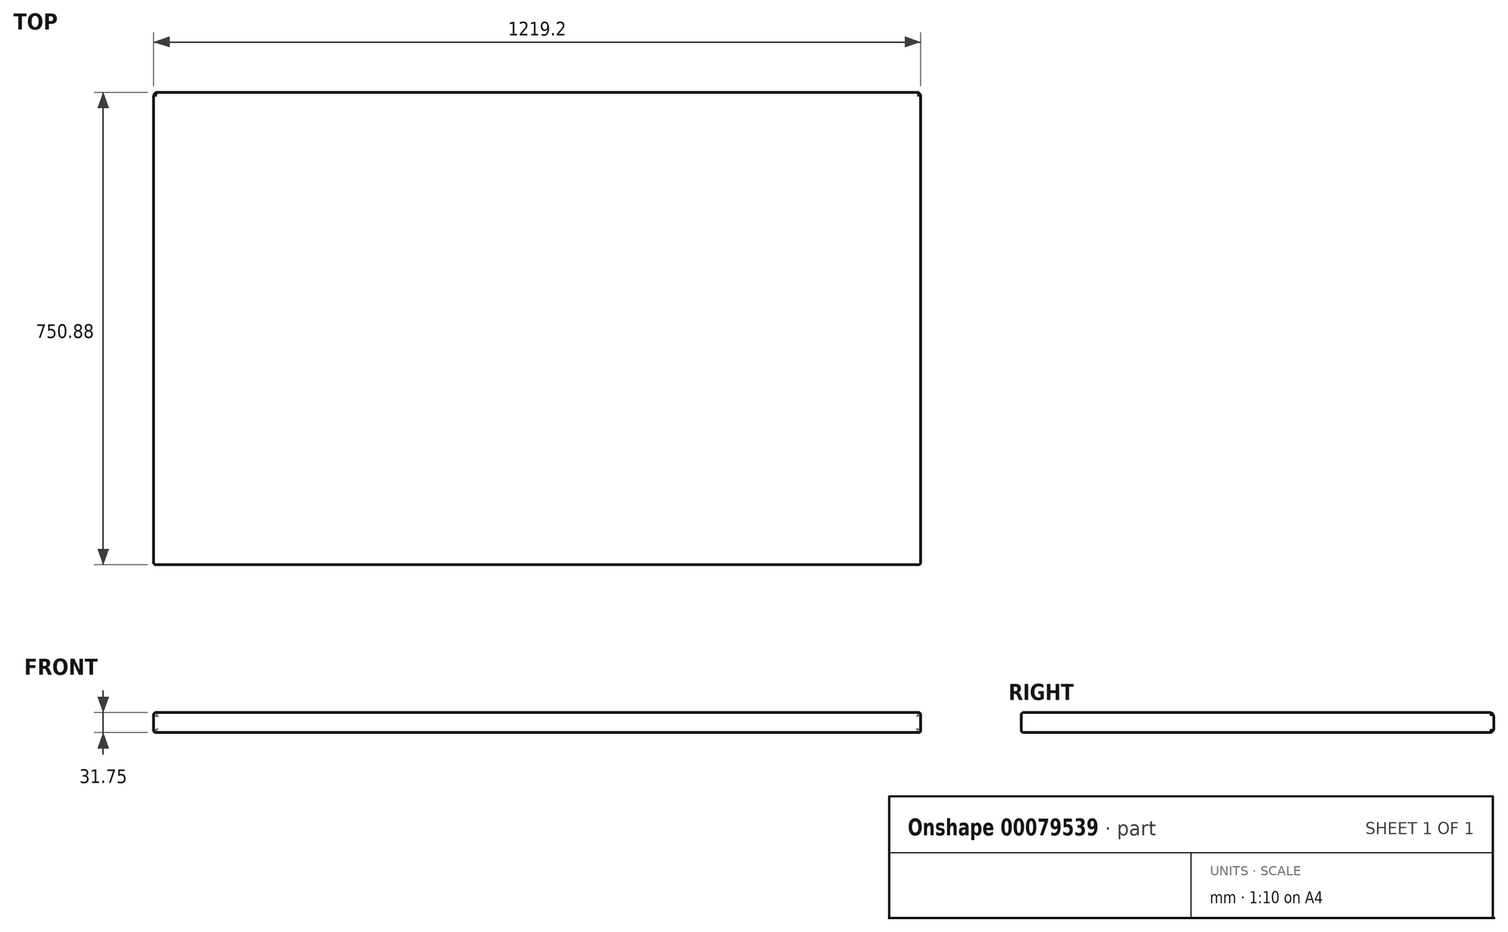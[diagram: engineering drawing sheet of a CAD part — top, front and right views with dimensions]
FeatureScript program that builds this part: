
annotation { "Feature Type Name" : "Feature", "Feature Type Description" : "" }
export const myFeature = defineFeature(function(context is Context, id is Id, definition is map)
    precondition{}
    {
        {
            var Q0;
            Q0=qCreatedBy(makeId("Top.planeOp"),FACE);
            var sketch = newSketch(context, id + "F0", { "sketchPlane" : qUnion([Q0])});
            skLineSegment(sketch, "E0.bottom", {"start": v(609.6, -375.44) * mm, "end": v(-609.6, -375.44) * mm});
            skLineSegment(sketch, "E0.top", {"start": v(609.6, 375.44) * mm, "end": v(-609.6, 375.44) * mm});
            skLineSegment(sketch, "E0.left", {"start": v(609.6, -375.44) * mm, "end": v(609.6, 375.44) * mm});
            skLineSegment(sketch, "E0.right", {"start": v(-609.6, -375.44) * mm, "end": v(-609.6, 375.44) * mm});
            skPoint(sketch, "E0.middle", {"position": v(0, 0) * mm});
            skSolve(sketch);
        }
        {
            var Q0;
            Q0=makeQuery(id+"F0.imprint","IMPRINT",FACE,{"disambiguationData":[TD([[makeQuery(id+"F0.imprint","IMPRINT",EDGE,{"derivedFrom":sQuery(id+"F0.wireOp",EDGE,"E0.bottom")}),-1.0]])]});
            extrude(context, id + "F1", {"entities" : qUnion([Q0]), "depth" : 31.75 * mm});
        }
        {
            var Q0;
            Q0=makeQuery(id+"F1.opExtrude","CAP_EDGE",EDGE,{"disambiguationData":[OSD([sQuery(id+"F0.wireOp",EDGE,"E0.right")])],"isStart":false});
            var Q1;
            Q1=makeQuery(id+"F1.opExtrude","CAP_EDGE",EDGE,{"disambiguationData":[OSD([sQuery(id+"F0.wireOp",EDGE,"E0.bottom")])],"isStart":false});
            var Q2;
            Q2=makeQuery(id+"F1.opExtrude","CAP_EDGE",EDGE,{"disambiguationData":[OSD([sQuery(id+"F0.wireOp",EDGE,"E0.left")])],"isStart":false});
            var Q3;
            Q3=makeQuery(id+"F1.opExtrude","CAP_EDGE",EDGE,{"disambiguationData":[OSD([sQuery(id+"F0.wireOp",EDGE,"E0.left")])],"isStart":true});
            var Q4;
            Q4=makeQuery(id+"F1.opExtrude","CAP_EDGE",EDGE,{"disambiguationData":[OSD([sQuery(id+"F0.wireOp",EDGE,"E0.bottom")])],"isStart":true});
            var Q5;
            Q5=makeQuery(id+"F1.opExtrude","CAP_EDGE",EDGE,{"disambiguationData":[OSD([sQuery(id+"F0.wireOp",EDGE,"E0.right")])],"isStart":true});
            var Q6;
            Q6=makeQuery(id+"F1.opExtrude","SWEPT_EDGE",EDGE,{"disambiguationData":[OSD([sQuery(id+"F0.wireOp",EDGE,"E0.bottom"),sQuery(id+"F0.wireOp",EDGE,"E0.right")])]});
            var Q7;
            Q7=makeQuery(id+"F1.opExtrude","SWEPT_EDGE",EDGE,{"disambiguationData":[OSD([sQuery(id+"F0.wireOp",EDGE,"E0.bottom"),sQuery(id+"F0.wireOp",EDGE,"E0.left")])]});
            fillet(context, id + "F2", {"entities" : qUnion([Q0, Q1, Q2, Q3, Q4, Q5, Q6, Q7]), "radius" : 3.17 * mm, "tangentPropagation" : true, "allowEdgeOverflow" : false});
        }
        {
            var Q0;
            Q0=makeQuery(id+"F1.opExtrude","CAP_EDGE",EDGE,{"disambiguationData":[OSD([sQuery(id+"F0.wireOp",EDGE,"E0.top")])],"isStart":true});
            var Q1;
            Q1=makeQuery(id+"F1.opExtrude","CAP_EDGE",EDGE,{"disambiguationData":[OSD([sQuery(id+"F0.wireOp",EDGE,"E0.top")])],"isStart":false});
            var Q2;
            Q2=makeQuery(id+"F1.opExtrude","SWEPT_EDGE",EDGE,{"disambiguationData":[OSD([sQuery(id+"F0.wireOp",EDGE,"E0.top"),sQuery(id+"F0.wireOp",EDGE,"E0.left")])]});
            var Q3;
            Q3=makeQuery(id+"F2.opFillet","BLEND_EDGE",EDGE,{"blendedFrom":[makeQuery(id+"F1.opExtrude","CAP_EDGE",EDGE,{"disambiguationData":[OSD([sQuery(id+"F0.wireOp",EDGE,"E0.left")])],"isStart":false}),makeQuery(id+"F1.opExtrude","SWEPT_FACE",FACE,{"disambiguationData":[OSD([sQuery(id+"F0.wireOp",EDGE,"E0.top")])]})],"blendedInto":[makeQuery(id+"F1.opExtrude","SWEPT_FACE",FACE,{"disambiguationData":[OSD([sQuery(id+"F0.wireOp",EDGE,"E0.top")])]})]});
            var Q4;
            Q4=makeQuery(id+"F2.opFillet","BLEND_EDGE",EDGE,{"blendedFrom":[makeQuery(id+"F1.opExtrude","CAP_EDGE",EDGE,{"disambiguationData":[OSD([sQuery(id+"F0.wireOp",EDGE,"E0.left")])],"isStart":true}),makeQuery(id+"F1.opExtrude","SWEPT_FACE",FACE,{"disambiguationData":[OSD([sQuery(id+"F0.wireOp",EDGE,"E0.top")])]})],"blendedInto":[makeQuery(id+"F1.opExtrude","SWEPT_FACE",FACE,{"disambiguationData":[OSD([sQuery(id+"F0.wireOp",EDGE,"E0.top")])]})]});
            var Q5;
            Q5=makeQuery(id+"F2.opFillet","BLEND_EDGE",EDGE,{"blendedFrom":[makeQuery(id+"F1.opExtrude","CAP_EDGE",EDGE,{"disambiguationData":[OSD([sQuery(id+"F0.wireOp",EDGE,"E0.right")])],"isStart":false}),makeQuery(id+"F1.opExtrude","SWEPT_FACE",FACE,{"disambiguationData":[OSD([sQuery(id+"F0.wireOp",EDGE,"E0.top")])]})],"blendedInto":[makeQuery(id+"F1.opExtrude","SWEPT_FACE",FACE,{"disambiguationData":[OSD([sQuery(id+"F0.wireOp",EDGE,"E0.top")])]})]});
            var Q6;
            Q6=makeQuery(id+"F1.opExtrude","SWEPT_EDGE",EDGE,{"disambiguationData":[OSD([sQuery(id+"F0.wireOp",EDGE,"E0.top"),sQuery(id+"F0.wireOp",EDGE,"E0.right")])]});
            var Q7;
            Q7=makeQuery(id+"F2.opFillet","BLEND_EDGE",EDGE,{"blendedFrom":[makeQuery(id+"F1.opExtrude","CAP_EDGE",EDGE,{"disambiguationData":[OSD([sQuery(id+"F0.wireOp",EDGE,"E0.right")])],"isStart":true}),makeQuery(id+"F1.opExtrude","SWEPT_FACE",FACE,{"disambiguationData":[OSD([sQuery(id+"F0.wireOp",EDGE,"E0.top")])]})],"blendedInto":[makeQuery(id+"F1.opExtrude","SWEPT_FACE",FACE,{"disambiguationData":[OSD([sQuery(id+"F0.wireOp",EDGE,"E0.top")])]})]});
            fillet(context, id + "F3", {"entities" : qUnion([Q0, Q1, Q2, Q3, Q4, Q5, Q6, Q7]), "radius" : 6.35 * mm, "tangentPropagation" : true, "allowEdgeOverflow" : false});
        }
    });
